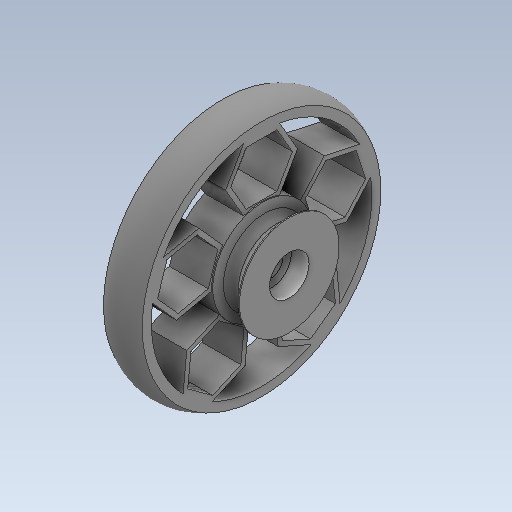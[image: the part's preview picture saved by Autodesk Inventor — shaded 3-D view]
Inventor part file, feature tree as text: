
AUTODESK INVENTOR PART (.ipt)
format: ipt  version: 2020 (Build 240168000, 168)  size: 319,488 bytes
history: native  units: in
note: dims shown in document units (in); Inventor stores cm internally (conversion verified against a paired STEP export)
features: sketch x4, other x3, extrude x3, revolve x1, projected_geometry x1
ambient origin geometry x8: Origin, YZ Plane, XZ Plane, XY Plane, X Axis, Y Axis, Z Axis, Center Point
bodies: Solid1 (feature_tree)
feature tree (12):
  other  "PulleyedWheelV1.ipt"
  extrude  "Extrusion1"  Depth=0.2756in
  extrude  "Extrusion2"  Depth=0.126in
  extrude  "Extrusion3"  Depth=0.126in
  revolve  "Revolution1"  [1 undecoded]
  other  "Solid1::PulleyedWheelV1.ipt"
  other  "TaggingFeature1"
  sketch  "Sketch1"  dims[d0=0.3937in]
  sketch  "Sketch2"  dims[d1=0.0394in d3=1.6929in d4=0.1181in d6=0.7087in d7=0.1969in d8=0.0in d9=1.6929in d10=0.063in d11=0.0315in d16=0.2756in d17=0.0in d20=0.0984in d24=0.0394in d26=45.0deg d2=0.2815in]
  sketch  "Sketch3"  dims[d5=0.126in d13=0.0in d15=0.2815in]
  sketch  "Sketch4"  dims[d18=0.126in d19=0.0in d21=0.1575in d23=0.0in d25=0.0in d28=45.0deg d29=90.0deg]
  projected_geometry  "Projected Loop1"
note: 1 required parameter value undecoded (feature->parameter linkage not recoverable at this tier; creation-order binding heuristic only, values carry confidence <= 0.55)
